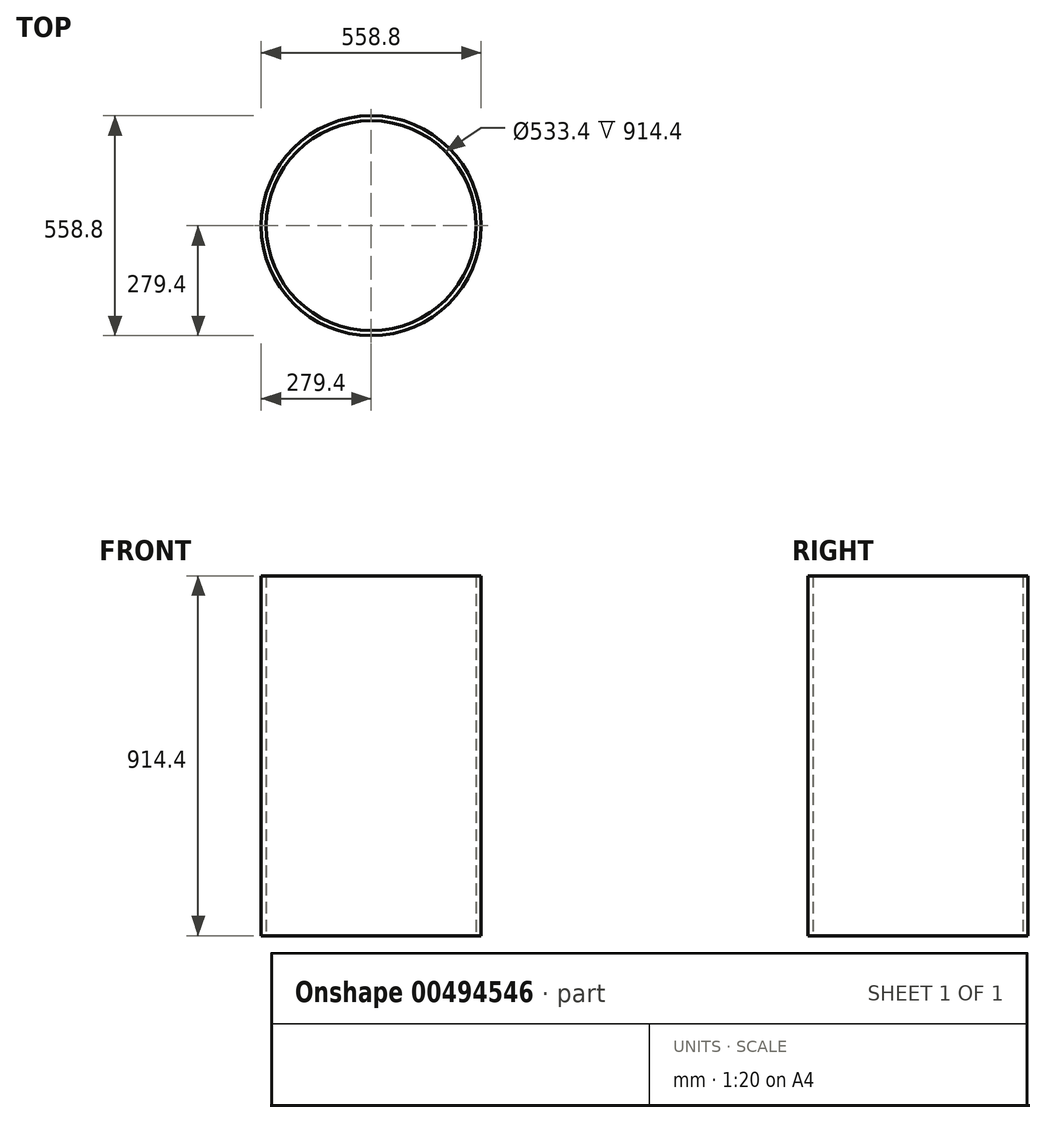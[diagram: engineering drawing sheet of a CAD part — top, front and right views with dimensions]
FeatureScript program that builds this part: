
annotation { "Feature Type Name" : "Feature", "Feature Type Description" : "" }
export const myFeature = defineFeature(function(context is Context, id is Id, definition is map)
    precondition{}
    {
        {
            var Q0;
            Q0=qCreatedBy(makeId("Top.planeOp"),FACE);
            var sketch = newSketch(context, id + "F0", { "sketchPlane" : qUnion([Q0])});
            skCircle(sketch, "E0", {"center": v(0, 0) * mm, "radius": 279.4 * mm});
            skCircle(sketch, "E1", {"center": v(0, 0) * mm, "radius": 266.7 * mm});
            skSolve(sketch);
        }
        {
            var Q0;
            Q0=qSketchRegion(id+"F0",true);
            extrude(context, id + "F1", {"entities" : qUnion([Q0]), "depth" : 914.4 * mm});
        }
    });
